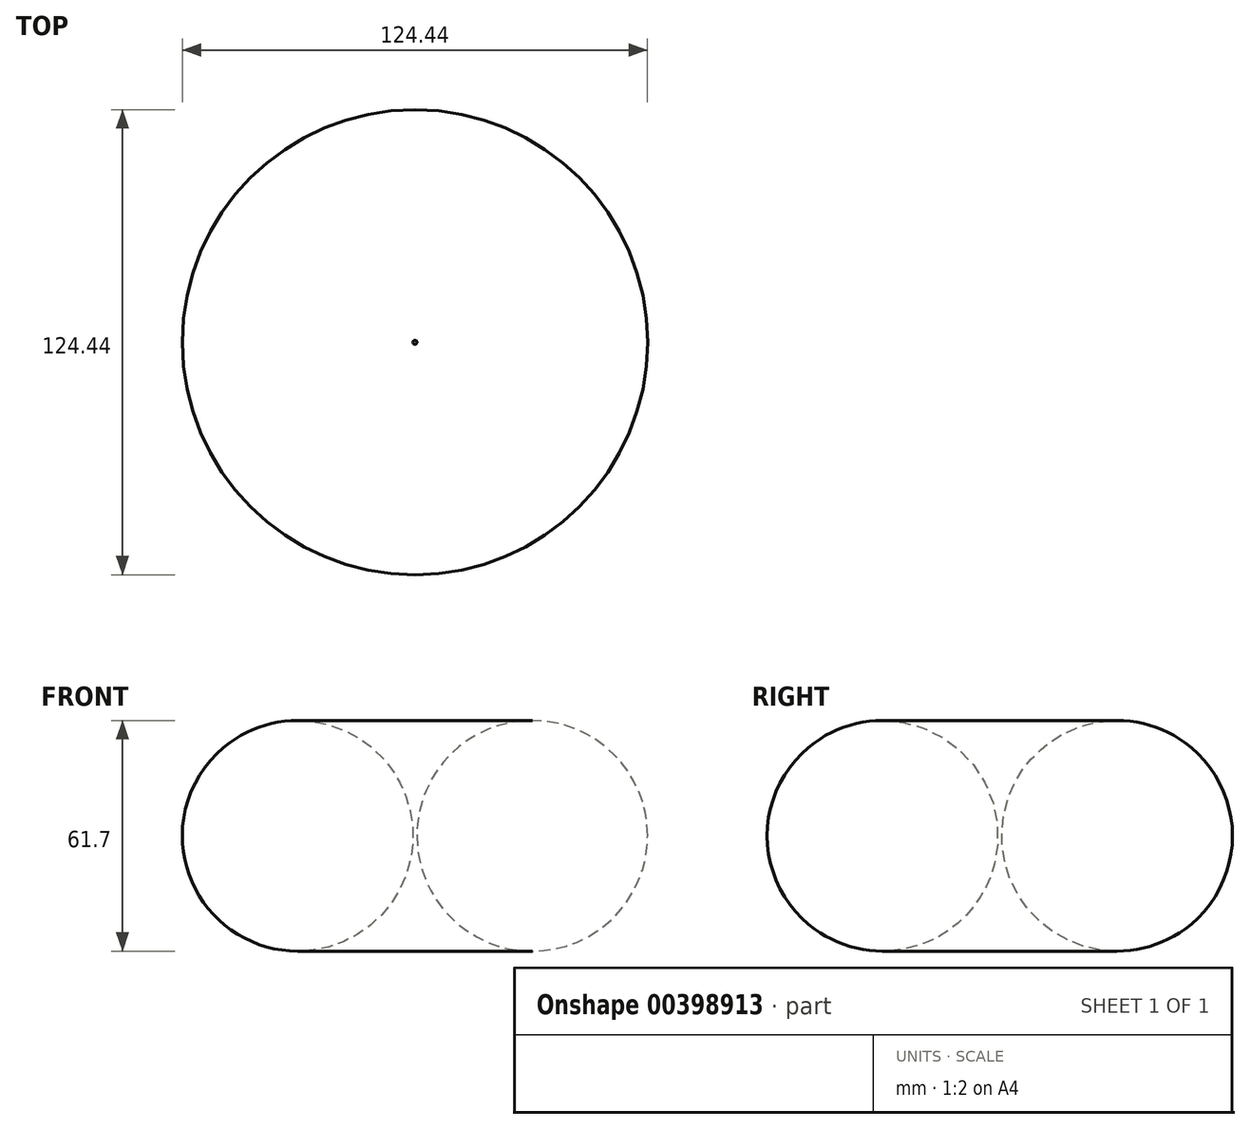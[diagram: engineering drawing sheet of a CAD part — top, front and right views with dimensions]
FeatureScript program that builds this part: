
annotation { "Feature Type Name" : "Feature", "Feature Type Description" : "" }
export const myFeature = defineFeature(function(context is Context, id is Id, definition is map)
    precondition{}
    {
        {
            var Q0;
            Q0=qCreatedBy(makeId("Front.planeOp"),FACE);
            var sketch = newSketch(context, id + "F0", { "sketchPlane" : qUnion([Q0])});
            skLineSegment(sketch, "E0", {"start": v(0, 62.74) * mm, "end": v(0, -49.25) * mm});
            skArc(sketch, "E1", {"start": v(-31.37, 0) * mm, "mid": v(-31.36, 0.93) * mm, "end": v(-31.32, 1.87) * mm});
            skCircle(sketch, "E2", {"center": v(-31.37, 0) * mm, "radius": 30.85 * mm});
            skSolve(sketch);
        }
        {
            var Q0;
            Q0=makeQuery(id+"F0.imprint","IMPRINT",FACE,{"disambiguationData":[TD([[makeQuery(id+"F0.imprint","IMPRINT",EDGE,{"derivedFrom":sQuery(id+"F0.wireOp",EDGE,"E2")}),1.0]])]});
            var Q1;
            Q1=sQuery(id+"F0.wireOp",EDGE,"E0");
            revolve(context, id + "F1", {"entities" : qUnion([Q0]), "axis" : qUnion([Q1]), "revolveType" : RevolveType.FULL});
        }
    });
